# Revit family: Door_Sliding-Bypass_1Lite-Frosted
name_source: partatom
category: Doors
units: mm (PartAtom-declared; Revit-internal decimal feet)

## family parameters
Always vertical = Yes
Classification Number = 23.30.10.17.11
Cut with Voids When Loaded = No
Host = Wall
Room Calculation Point = No
Shared = No

## types (3) — shared parameters
3Pnl = No
4pnl = No
Assembly Code = C1020110
Description = Sliding Bypass Door as Specified
Exterior Trim = Wood_Pine_Painted-Color as Specified
Floor Gap = 0' - 0 3/4"
Frame Projection Ext. = 0' - 1"
Frame Projection Int. = 0' - 1"
Frame Width = 0' - 3"
Function = Interior
Head Gap = 0' - 1"
Height = 7' - 0"
Interior Trim = Wood_Pine_Painted-Color as Specified
Jamb Material = Wood_Pine_Painted-Color as Specified
Keynote = 08 32 13
Manufacturer = Renin Canada Corp.
Manufacturer Fax = 905-791-3813
Manufacturer Website = http://www.eriashomedesigns.com
Operation = Sliding
Panel = Panel_1Lite : Panel
Panel Count = 2
Panel Finish = Glass_Tempered_Frosted
Panel Thickness = 0' - 0 1/4"
Panel Width = 4' - 0"
Product Data = http://www.arcat.com
Revision = R1_01-2016
Rough Height = 7' - 1"
Rough Opening Gap = 0' - 0 1/4"
Rough Width = 8' - 2"
Sales Information = http://www.eriashomedesigns.com
Show Trim = Yes
Specification = http://www.arcat.com
Stile Thickness = 0' - 2"
Thickness = 0' - 1 3/8"
Threshold Depth = 0' - 3 1/2"
Total Opening Height = 7' - 1 3/4"
Trim Reveal = 0' - 0 1/16"
URL = http://www.eriashomedesigns.com
Wall Closure = By host
Width = 8' - 0"
_Jamb Thickness = 0' - 0 3/4"
spread = 0' - 1 9/16"

## per-type parameters (varying)
| type | Frame Finish | Threshold Finish |
| 2000 | Wood - Renin - Cherry | Wood - Renin - Cherry |
| 2230 | Wood - Renin - Espresso | Wood - Renin - Espresso |
| 2010 | Metal - Renin - Off-White | Metal - Renin - Off-White |

note: column(s) folded — value = type name in every type: Model

## geometry (parser evidence)
native form markers: Blend x22, Sweep x9
no freeform markers — native parametric forms only
